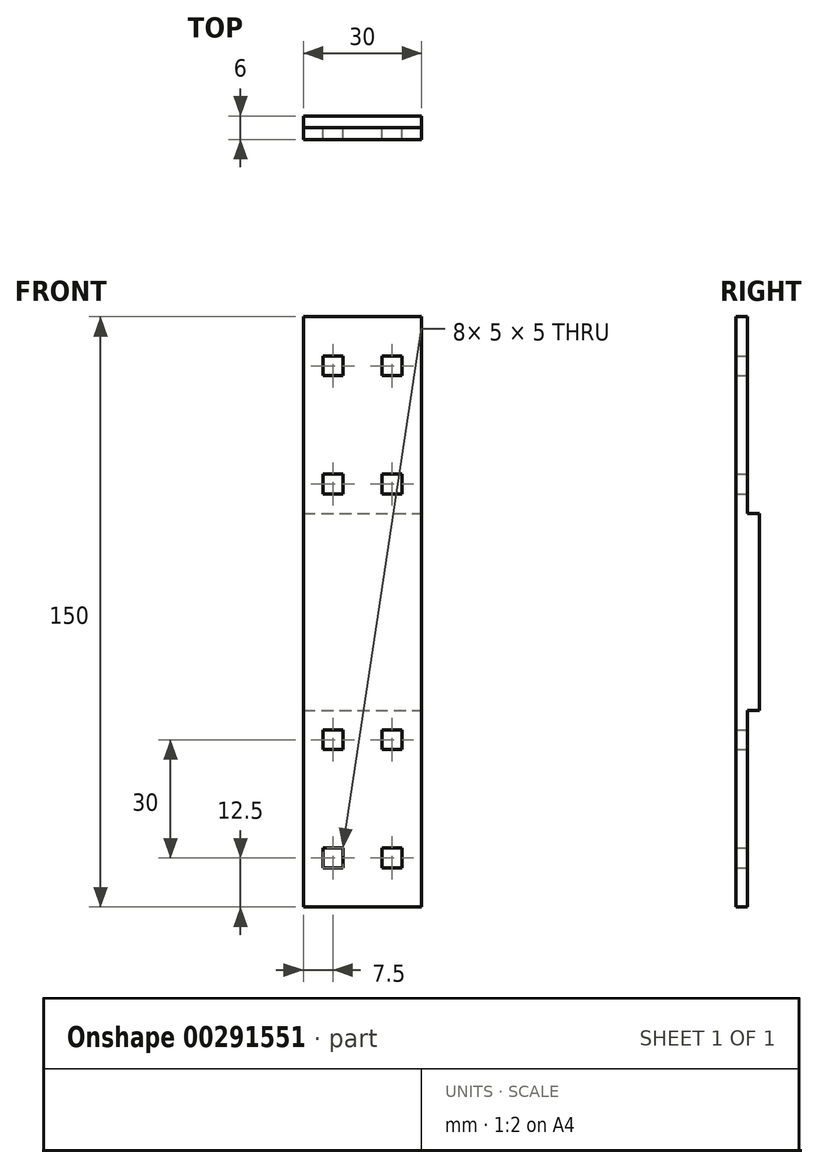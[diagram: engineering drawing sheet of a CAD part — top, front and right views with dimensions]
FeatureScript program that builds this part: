
annotation { "Feature Type Name" : "Feature", "Feature Type Description" : "" }
export const myFeature = defineFeature(function(context is Context, id is Id, definition is map)
    precondition{}
    {
        {
            var Q0;
            Q0=qCreatedBy(makeId("Top.planeOp"),FACE);
            var sketch = newSketch(context, id + "F0", { "sketchPlane" : qUnion([Q0])});
            skLineSegment(sketch, "E0.bottom", {"start": v(-15, 3) * mm, "end": v(15, 3) * mm});
            skLineSegment(sketch, "E0.top", {"start": v(-15, -3) * mm, "end": v(15, -3) * mm});
            skLineSegment(sketch, "E0.left", {"start": v(-15, 3) * mm, "end": v(-15, -3) * mm});
            skLineSegment(sketch, "E0.right", {"start": v(15, 3) * mm, "end": v(15, -3) * mm});
            skSolve(sketch);
        }
        {
            var Q0;
            Q0=qSketchRegion(id+"F0",true);
            extrude(context, id + "F1", {"entities" : qUnion([Q0]), "depth" : 150 * mm, "offsetDistance" : 25 * mm});
        }
        {
            var Q0;
            Q0=makeQuery(id+"F1.opExtrude","SWEPT_FACE",FACE,{"disambiguationData":[OSD([sQuery(id+"F0.wireOp",EDGE,"E0.right")])]});
            var sketch = newSketch(context, id + "F2", { "sketchPlane" : qUnion([Q0])});
            skLineSegment(sketch, "E1.bottom", {"start": v(0, 150) * mm, "end": v(3, 150) * mm});
            skLineSegment(sketch, "E1.top", {"start": v(0, 100) * mm, "end": v(3, 100) * mm});
            skLineSegment(sketch, "E1.left", {"start": v(0, 150) * mm, "end": v(0, 100) * mm});
            skLineSegment(sketch, "E1.right", {"start": v(3, 150) * mm, "end": v(3, 100) * mm});
            skLineSegment(sketch, "E2.MirrorCS", {"start": v(0, 0) * mm, "end": v(3, 0) * mm});
            skLineSegment(sketch, "E3.MirrorCS", {"start": v(0, 50) * mm, "end": v(3, 50) * mm});
            skLineSegment(sketch, "E4.MirrorCS", {"start": v(0, 0) * mm, "end": v(0, 50) * mm});
            skLineSegment(sketch, "E5.MirrorCS", {"start": v(3, 0) * mm, "end": v(3, 50) * mm});
            skSolve(sketch);
        }
        {
            var Q0;
            Q0=qSketchRegion(id+"F2",true);
            extrude(context, id + "F3", {"entities" : qUnion([Q0]), "operationType" : NewBodyOperationType.REMOVE, "endBound" : BoundingType.UP_TO_NEXT, "oppositeDirection" : true, "depth" : 25 * mm, "offsetDistance" : 25 * mm});
        }
        {
            var Q0;
            Q0=makeQuery(id+"F3.boolean.opBoolean","COPY",FACE,{"derivedFrom":makeQuery(id+"F3.opExtrude","SWEPT_FACE",FACE,{"disambiguationData":[OSD([sQuery(id+"F2.wireOp",EDGE,"E1.left")])]})});
            var sketch = newSketch(context, id + "F4", { "sketchPlane" : qUnion([Q0])});
            skLineSegment(sketch, "E6.bottom", {"start": v(5, 15) * mm, "end": v(10, 15) * mm});
            skLineSegment(sketch, "E6.top", {"start": v(5, 10) * mm, "end": v(10, 10) * mm});
            skLineSegment(sketch, "E6.left", {"start": v(5, 15) * mm, "end": v(5, 10) * mm});
            skLineSegment(sketch, "E6.right", {"start": v(10, 15) * mm, "end": v(10, 10) * mm});
            skLineSegment(sketch, "E7.MirrorCS", {"start": v(-5, 10) * mm, "end": v(-10, 10) * mm});
            skLineSegment(sketch, "E8.MirrorCS", {"start": v(-5, 15) * mm, "end": v(-5, 10) * mm});
            skLineSegment(sketch, "E9.MirrorCS", {"start": v(-10, 15) * mm, "end": v(-10, 10) * mm});
            skLineSegment(sketch, "E10.MirrorCS", {"start": v(-5, 15) * mm, "end": v(-10, 15) * mm});
            skLineSegment(sketch, "E11.MirrorCS", {"start": v(-5, 40) * mm, "end": v(-5, 45) * mm});
            skLineSegment(sketch, "E12.MirrorCS", {"start": v(-5, 45) * mm, "end": v(-10, 45) * mm});
            skLineSegment(sketch, "E13.MirrorCS", {"start": v(5, 40) * mm, "end": v(10, 40) * mm});
            skLineSegment(sketch, "E14.MirrorCS", {"start": v(5, 45) * mm, "end": v(10, 45) * mm});
            skLineSegment(sketch, "E15.MirrorCS", {"start": v(5, 40) * mm, "end": v(5, 45) * mm});
            skLineSegment(sketch, "E16.MirrorCS", {"start": v(10, 40) * mm, "end": v(10, 45) * mm});
            skLineSegment(sketch, "E17.MirrorCS", {"start": v(-5, 40) * mm, "end": v(-10, 40) * mm});
            skLineSegment(sketch, "E18.MirrorCS", {"start": v(-10, 40) * mm, "end": v(-10, 45) * mm});
            skLineSegment(sketch, "E19.MirrorCS", {"start": v(5, 110) * mm, "end": v(5, 105) * mm});
            skLineSegment(sketch, "E20.MirrorCS", {"start": v(5, 105) * mm, "end": v(10, 105) * mm});
            skLineSegment(sketch, "E21.MirrorCS", {"start": v(5, 110) * mm, "end": v(10, 110) * mm});
            skLineSegment(sketch, "E22.MirrorCS", {"start": v(-5, 105) * mm, "end": v(-10, 105) * mm});
            skLineSegment(sketch, "E23.MirrorCS", {"start": v(-5, 110) * mm, "end": v(-5, 105) * mm});
            skLineSegment(sketch, "E24.MirrorCS", {"start": v(-10, 110) * mm, "end": v(-10, 105) * mm});
            skLineSegment(sketch, "E25.MirrorCS", {"start": v(-5, 135) * mm, "end": v(-10, 135) * mm});
            skLineSegment(sketch, "E26.MirrorCS", {"start": v(-5, 140) * mm, "end": v(-10, 140) * mm});
            skLineSegment(sketch, "E27.MirrorCS", {"start": v(10, 135) * mm, "end": v(10, 140) * mm});
            skLineSegment(sketch, "E28.MirrorCS", {"start": v(5, 135) * mm, "end": v(5, 140) * mm});
            skLineSegment(sketch, "E29.MirrorCS", {"start": v(10, 110) * mm, "end": v(10, 105) * mm});
            skLineSegment(sketch, "E30.MirrorCS", {"start": v(5, 135) * mm, "end": v(10, 135) * mm});
            skLineSegment(sketch, "E31.MirrorCS", {"start": v(-5, 110) * mm, "end": v(-10, 110) * mm});
            skLineSegment(sketch, "E32.MirrorCS", {"start": v(-10, 135) * mm, "end": v(-10, 140) * mm});
            skLineSegment(sketch, "E33.MirrorCS", {"start": v(-5, 135) * mm, "end": v(-5, 140) * mm});
            skLineSegment(sketch, "E34.MirrorCS", {"start": v(5, 140) * mm, "end": v(10, 140) * mm});
            skSolve(sketch);
        }
        {
            var Q0;
            Q0=qSketchRegion(id+"F4",true);
            extrude(context, id + "F5", {"entities" : qUnion([Q0]), "operationType" : NewBodyOperationType.REMOVE, "endBound" : BoundingType.UP_TO_NEXT, "oppositeDirection" : true, "depth" : 25 * mm, "offsetDistance" : 25 * mm});
        }
    });
